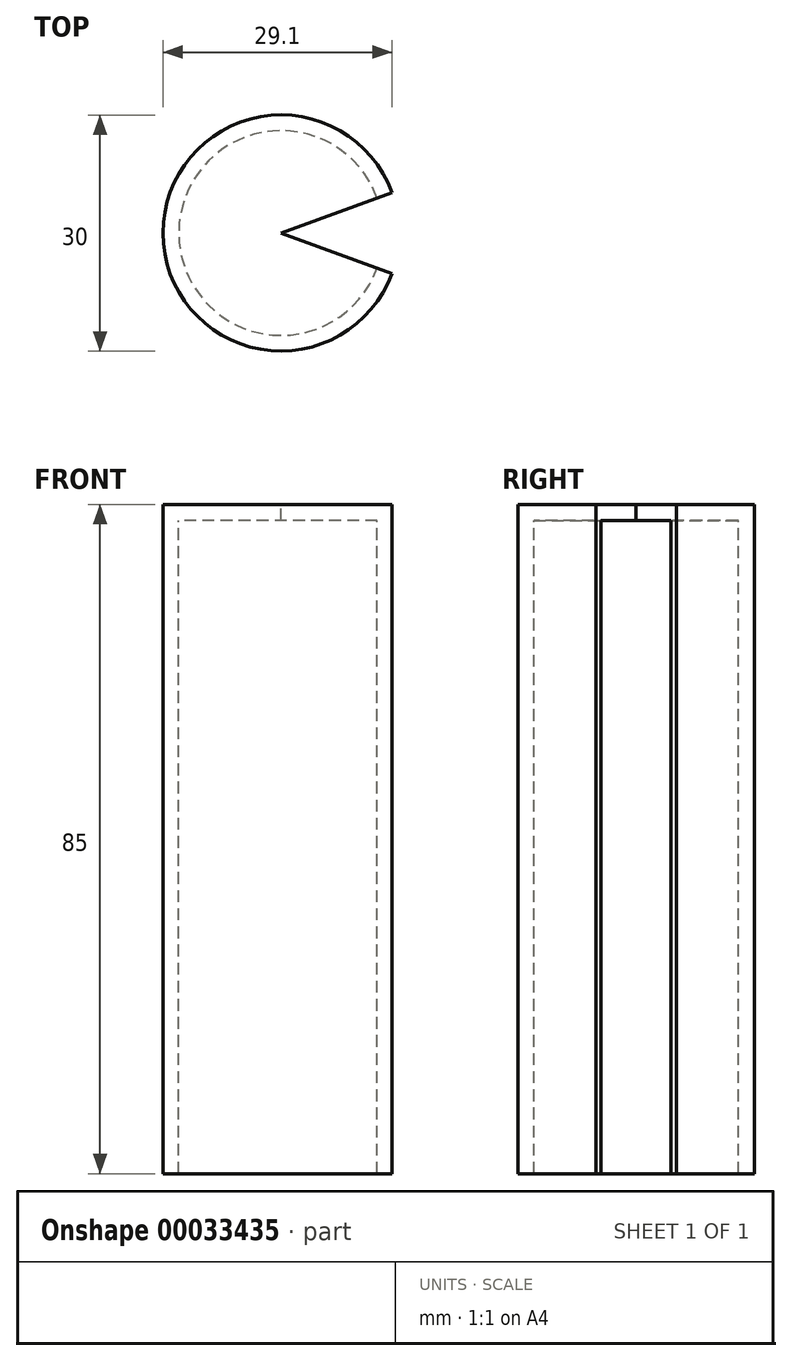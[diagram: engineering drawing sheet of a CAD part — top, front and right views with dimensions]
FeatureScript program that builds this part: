
annotation { "Feature Type Name" : "Feature", "Feature Type Description" : "" }
export const myFeature = defineFeature(function(context is Context, id is Id, definition is map)
    precondition{}
    {
        {
            var Q0;
            Q0=qCreatedBy(makeId("Front.planeOp"),FACE);
            var sketch = newSketch(context, id + "F0", { "sketchPlane" : qUnion([Q0])});
            skLineSegment(sketch, "E0", {"start": v(0, 44.5) * mm, "end": v(0, -49.7) * mm, "construction": true});
            skLineSegment(sketch, "E1", {"start": v(0, 38.26) * mm, "end": v(-15, 38.26) * mm});
            skLineSegment(sketch, "E2", {"start": v(-15, 38.26) * mm, "end": v(-15, -46.74) * mm});
            skLineSegment(sketch, "E3", {"start": v(-15, -46.74) * mm, "end": v(-13, -46.74) * mm});
            skLineSegment(sketch, "E4", {"start": v(-13, -46.74) * mm, "end": v(-13, 36.26) * mm});
            skLineSegment(sketch, "E5", {"start": v(-13, 36.26) * mm, "end": v(0, 36.26) * mm});
            skLineSegment(sketch, "E6", {"start": v(0, 36.26) * mm, "end": v(0, 38.26) * mm});
            skSolve(sketch);
        }
        {
            var Q0;
            Q0=qCreatedBy(makeId("Right.planeOp"),FACE);
            var sketch = newSketch(context, id + "F1", { "sketchPlane" : qUnion([Q0])});
            skLineSegment(sketch, "E7", {"start": v(0, 44.43) * mm, "end": v(0, -62.33) * mm});
            skSolve(sketch);
        }
        {
            var Q0;
            Q0=makeQuery(id+"F0.imprint","IMPRINT",FACE,{"disambiguationData":[TD([[makeQuery(id+"F0.imprint","IMPRINT",EDGE,{"derivedFrom":sQuery(id+"F0.wireOp",EDGE,"E1")}),1.0]])]});
            var Q1;
            Q1=sQuery(id+"F1.wireOp",EDGE,"E7");
            revolve(context, id + "F2", {"entities" : qUnion([Q0]), "axis" : qUnion([Q1]), "revolveType" : RevolveType.SYMMETRIC, "angle" : 320 * degree});
        }
    });
